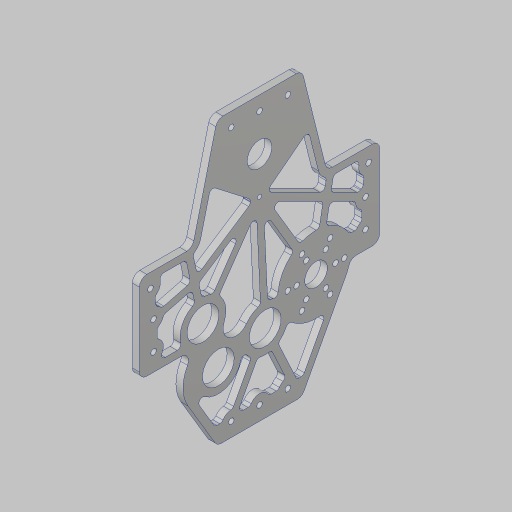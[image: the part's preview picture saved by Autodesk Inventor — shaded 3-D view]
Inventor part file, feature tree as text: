
AUTODESK INVENTOR PART (.ipt)
format: ipt  version: 2023.5 (Build 275446000, 446)  size: 760,832 bytes
history: native  units: in
note: dims shown in document units (in); Inventor stores cm internally (conversion verified against a paired STEP export)
features: sketch x4, hole x3, extrude x2, fillet x2, projected_geometry x2
ambient origin geometry x8: Origin, YZ Plane, XZ Plane, XY Plane, X Axis, Y Axis, Z Axis, Center Point
bodies: Solid1 (feature_tree)
feature tree (13):
  sketch  "Sketch1"  dims[d0=10.0in d1=1.0in]
  sketch  "Sketch2"  dims[d2=3.25in d3=1.0in]
  extrude  "Extrusion1"  Depth=10.0in
  hole  "Mount Holes"  [1 undecoded]
  hole  "Motor Mount Holes"  [1 undecoded]
  fillet  "Fillet1"  Radius=0.123in
  hole  "Hole4"  [1 undecoded]
  extrude  "Extrusion4"  Depth=0.13in
  fillet  "Fillet3"  Radius=3.3in
  sketch  "Sketch8"  dims[d4=1.942in d6=3.5in d7=0.123in]
  sketch  "Sketch9"  dims[d8=1.0in d9=1.0in d10=0.6in d11=3.3in d12=0.9in d13=2.5in d14=1.2in d15=2.2in d16=2.4in d19=2.5in d23=0.8in d24=1.125in d26=1.0in d27=1.0in d28=1.0in d29=1.0in d30=0.25in d31=0.25in d32=0.25in d33=1.375in d34=2.0in d35=2.3622in d37=360.0deg d41=0.125in d42=3.0in d44=0.25in d45=0.0in d46=0.201in d47=0.75in d48=0.385in d49=0.25in d50=0.5635in d51=1.0in d52=0.8108in d53=0.201in d54=0.75in d55=0.375in d56=0.25in d57=0.5635in d58=1.0in d59=0.8108in d60=4.006in d63=1.25in d64=1.75in d66=1.375in d67=1.25in d68=0.875in d70=0.375in d71=1.875in d73=4.6532in d74=0.5in d75=1.432in d76=4.297in d77=0.26in d78=0.391in d79=0.391in d123=4.651in d133=8.0944in d134=1.8013in d135=4.4272in d141=0.875in d162=2.624in d163=0.156in d164=0.38in d165=0.385in d166=0.25in d167=0.5635in d168=1.0in d169=0.8108in d170=0.25in d171=0.25in d172=0.25in d173=0.25in d174=0.25in d175=0.25in d176=0.25in d177=0.25in d178=0.25in d179=0.25in d180=0.25in d181=0.25in d182=0.25in d183=0.25in d184=0.25in d185=0.25in d186=0.125in d187=0.125in d188=0.125in d189=0.125in d190=0.125in d191=0.125in d192=0.125in d193=0.125in d194=0.125in d195=0.125in d196=0.125in d197=0.125in d198=0.125in d199=0.125in d200=0.125in d201=0.125in d202=0.125in d203=0.125in d204=0.125in d205=0.125in d207=0.0in d208=0.0in d209=0.13in d210=0.125in d211=0.125in]
  projected_geometry  "Project Cut Edges5"
  projected_geometry  "Project Cut Edges6"
note: 3 required parameter values undecoded (feature->parameter linkage not recoverable at this tier; creation-order binding heuristic only, values carry confidence <= 0.55)
